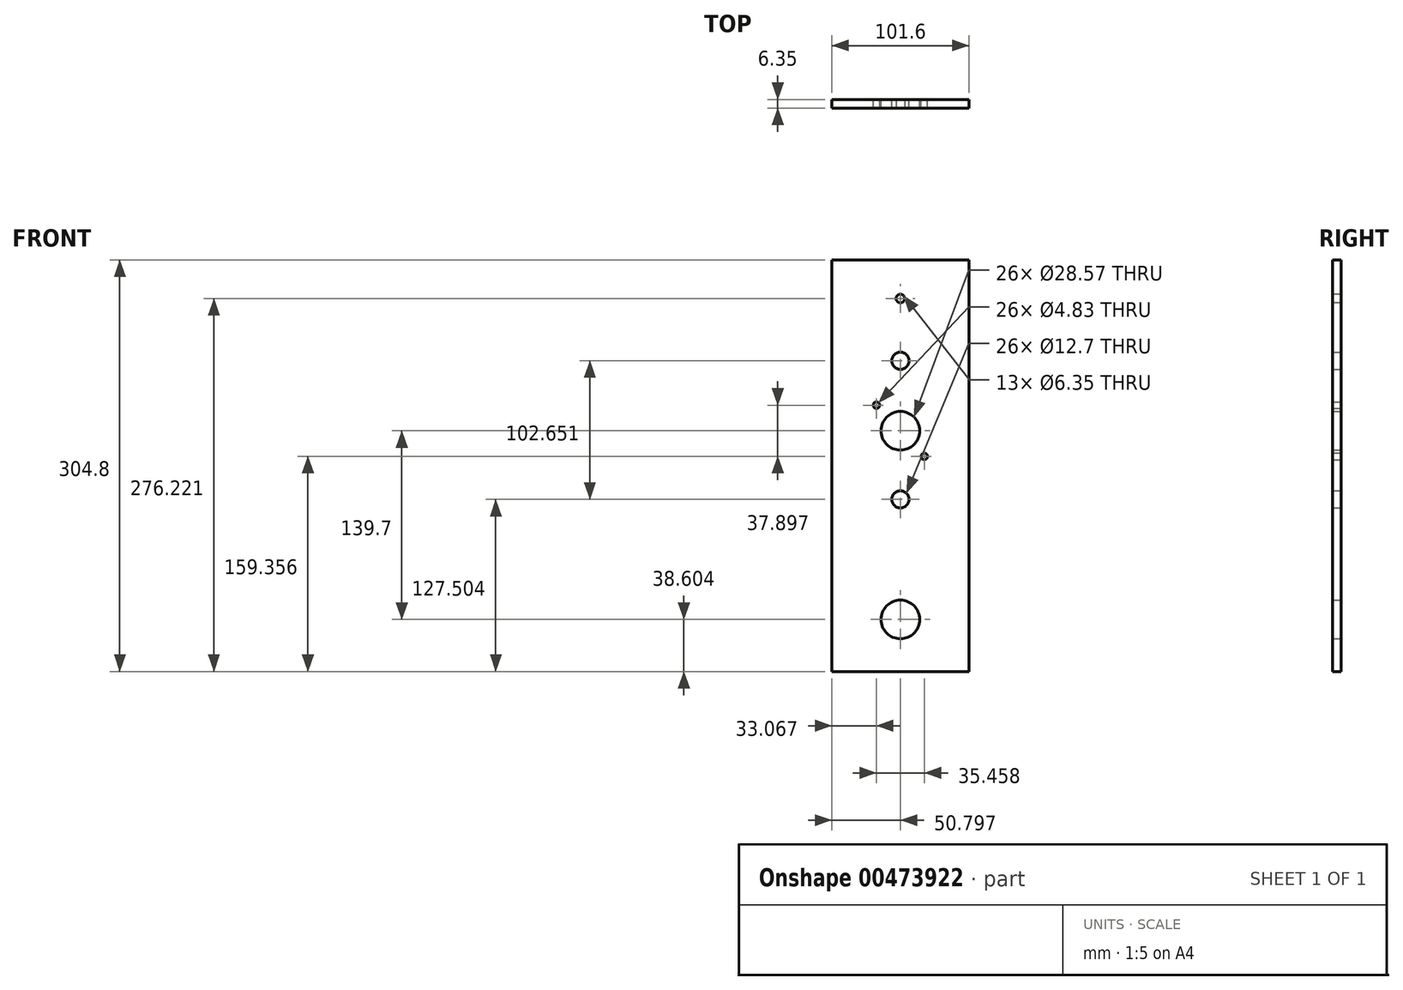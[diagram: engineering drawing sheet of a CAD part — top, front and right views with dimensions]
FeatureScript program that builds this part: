
annotation { "Feature Type Name" : "Feature", "Feature Type Description" : "" }
export const myFeature = defineFeature(function(context is Context, id is Id, definition is map)
    precondition{}
    {
        {
            var Q0;
            Q0=qCreatedBy(makeId("Front.planeOp"),FACE);
            var sketch = newSketch(context, id + "F0", { "sketchPlane" : qUnion([Q0])});
            skLineSegment(sketch, "E0.bottom", {"start": v(51.22, 243.74) * mm, "end": v(152.82, 243.74) * mm});
            skLineSegment(sketch, "E0.top", {"start": v(51.22, -61.06) * mm, "end": v(152.82, -61.06) * mm});
            skLineSegment(sketch, "E0.left", {"start": v(51.22, 243.74) * mm, "end": v(51.22, -61.06) * mm});
            skLineSegment(sketch, "E0.right", {"start": v(152.82, 243.74) * mm, "end": v(152.82, -61.06) * mm});
            skSolve(sketch);
        }
        {
            var Q0;
            Q0=makeQuery(id+"F0.imprint","IMPRINT",FACE,{"disambiguationData":[TD([[makeQuery(id+"F0.imprint","IMPRINT",EDGE,{"derivedFrom":sQuery(id+"F0.wireOp",EDGE,"E0.bottom")}),-1.0]])]});
            extrude(context, id + "F1", {"entities" : qUnion([Q0]), "depth" : 6.35 * mm});
        }
        {
            var Q0;
            Q0=makeQuery(id+"F1.opExtrude","CAP_FACE",FACE,{"disambiguationData":[OSD([sQuery(id+"F0.wireOp",EDGE,"E0.bottom"),sQuery(id+"F0.wireOp",EDGE,"E0.top"),sQuery(id+"F0.wireOp",EDGE,"E0.left"),sQuery(id+"F0.wireOp",EDGE,"E0.right")])],"isStart":false});
            var sketch = newSketch(context, id + "F2", { "sketchPlane" : qUnion([Q0])});
            skCircle(sketch, "E1", {"center": v(102.02, 215.16) * mm, "radius": 3.18 * mm});
            skSolve(sketch);
        }
        {
            var Q0;
            Q0=makeQuery(id+"F2.imprint","IMPRINT",FACE,{"disambiguationData":[TD([[makeQuery(id+"F2.imprint","IMPRINT",EDGE,{"derivedFrom":sQuery(id+"F2.wireOp",EDGE,"E1")}),1.0]])]});
            extrude(context, id + "F3", {"entities" : qUnion([Q0]), "operationType" : NewBodyOperationType.REMOVE, "oppositeDirection" : true, "depth" : 6.35 * mm});
        }
        {
            var Q0;
            Q0=makeQuery(id+"F1.opExtrude","CAP_FACE",FACE,{"disambiguationData":[OSD([sQuery(id+"F0.wireOp",EDGE,"E0.bottom"),sQuery(id+"F0.wireOp",EDGE,"E0.top"),sQuery(id+"F0.wireOp",EDGE,"E0.left"),sQuery(id+"F0.wireOp",EDGE,"E0.right")])],"isStart":true});
            var sketch = newSketch(context, id + "F4", { "sketchPlane" : qUnion([Q0])});
            skCircle(sketch, "E2", {"center": v(-102.02, -22.46) * mm, "radius": 14.29 * mm});
            skSolve(sketch);
        }
        {
            var Q0;
            Q0=makeQuery(id+"F4.imprint","IMPRINT",FACE,{"disambiguationData":[TD([[makeQuery(id+"F4.imprint","IMPRINT",EDGE,{"derivedFrom":sQuery(id+"F4.wireOp",EDGE,"E2")}),1.0]])]});
            extrude(context, id + "F5", {"entities" : qUnion([Q0]), "operationType" : NewBodyOperationType.REMOVE, "oppositeDirection" : true, "depth" : 6.35 * mm});
        }
        {
            var Q0;
            Q0=makeQuery(id+"F1.opExtrude","CAP_FACE",FACE,{"disambiguationData":[OSD([sQuery(id+"F0.wireOp",EDGE,"E0.bottom"),sQuery(id+"F0.wireOp",EDGE,"E0.top"),sQuery(id+"F0.wireOp",EDGE,"E0.left"),sQuery(id+"F0.wireOp",EDGE,"E0.right")])],"isStart":true});
            var sketch = newSketch(context, id + "F6", { "sketchPlane" : qUnion([Q0])});
            skCircle(sketch, "E3", {"center": v(-102.02, 117.24) * mm, "radius": 14.29 * mm});
            skSolve(sketch);
        }
        {
            var Q0;
            Q0=makeQuery(id+"F6.imprint","IMPRINT",FACE,{"disambiguationData":[TD([[makeQuery(id+"F6.imprint","IMPRINT",EDGE,{"derivedFrom":sQuery(id+"F6.wireOp",EDGE,"E3")}),1.0]])]});
            extrude(context, id + "F7", {"entities" : qUnion([Q0]), "operationType" : NewBodyOperationType.REMOVE, "oppositeDirection" : true, "depth" : 6.35 * mm});
        }
        {
            var Q0;
            Q0=makeQuery(id+"F4.imprint","IMPRINT",FACE,{"disambiguationData":[TD([[makeQuery(id+"F4.imprint","IMPRINT",EDGE,{"derivedFrom":sQuery(id+"F4.wireOp",EDGE,"E2")}),-1.0]])]});
            var sketch = newSketch(context, id + "F8", { "sketchPlane" : qUnion([Q0])});
            skLineSegment(sketch, "E4.bottom", {"start": v(-79.8, 139.47) * mm, "end": v(-124.24, 139.47) * mm});
            skLineSegment(sketch, "E4.top", {"start": v(-79.8, 95.02) * mm, "end": v(-124.24, 95.02) * mm});
            skLineSegment(sketch, "E4.left", {"start": v(-79.8, 139.47) * mm, "end": v(-79.8, 95.02) * mm});
            skLineSegment(sketch, "E4.right", {"start": v(-124.24, 139.47) * mm, "end": v(-124.24, 95.02) * mm});
            skCircle(sketch, "E5", {"center": v(-84.29, 136.2) * mm, "radius": 2.41 * mm});
            skCircle(sketch, "E6", {"center": v(-119.75, 98.3) * mm, "radius": 2.41 * mm});
            skSolve(sketch);
        }
        {
            var Q0;
            Q0=makeQuery(id+"F8.imprint","IMPRINT",FACE,{"disambiguationData":[TD([[makeQuery(id+"F8.imprint","IMPRINT",EDGE,{"derivedFrom":sQuery(id+"F8.wireOp",EDGE,"E5")}),1.0]])]});
            var Q1;
            Q1=makeQuery(id+"F8.imprint","IMPRINT",FACE,{"disambiguationData":[TD([[makeQuery(id+"F8.imprint","IMPRINT",EDGE,{"derivedFrom":sQuery(id+"F8.wireOp",EDGE,"E6")}),1.0]])]});
            extrude(context, id + "F9", {"entities" : qUnion([Q0, Q1]), "operationType" : NewBodyOperationType.REMOVE, "oppositeDirection" : true, "depth" : 6.35 * mm});
        }
        {
            var Q0;
            Q0=makeQuery(id+"F6.imprint","IMPRINT",FACE,{"disambiguationData":[TD([[makeQuery(id+"F6.imprint","IMPRINT",EDGE,{"derivedFrom":sQuery(id+"F6.wireOp",EDGE,"E3")}),-1.0]])]});
            var sketch = newSketch(context, id + "F10", { "sketchPlane" : qUnion([Q0])});
            skCircle(sketch, "E7", {"center": v(-102.02, 169.1) * mm, "radius": 6.35 * mm});
            skCircle(sketch, "E8", {"center": v(-102.02, 66.44) * mm, "radius": 6.35 * mm});
            skSolve(sketch);
        }
        {
            var Q0;
            Q0=makeQuery(id+"F10.imprint","IMPRINT",FACE,{"disambiguationData":[TD([[makeQuery(id+"F10.imprint","IMPRINT",EDGE,{"derivedFrom":sQuery(id+"F10.wireOp",EDGE,"E8")}),1.0]])]});
            var Q1;
            Q1=makeQuery(id+"F10.imprint","IMPRINT",FACE,{"disambiguationData":[TD([[makeQuery(id+"F10.imprint","IMPRINT",EDGE,{"derivedFrom":sQuery(id+"F10.wireOp",EDGE,"E7")}),1.0]])]});
            extrude(context, id + "F11", {"entities" : qUnion([Q0, Q1]), "operationType" : NewBodyOperationType.REMOVE, "oppositeDirection" : true, "depth" : 6.35 * mm});
        }
    });
